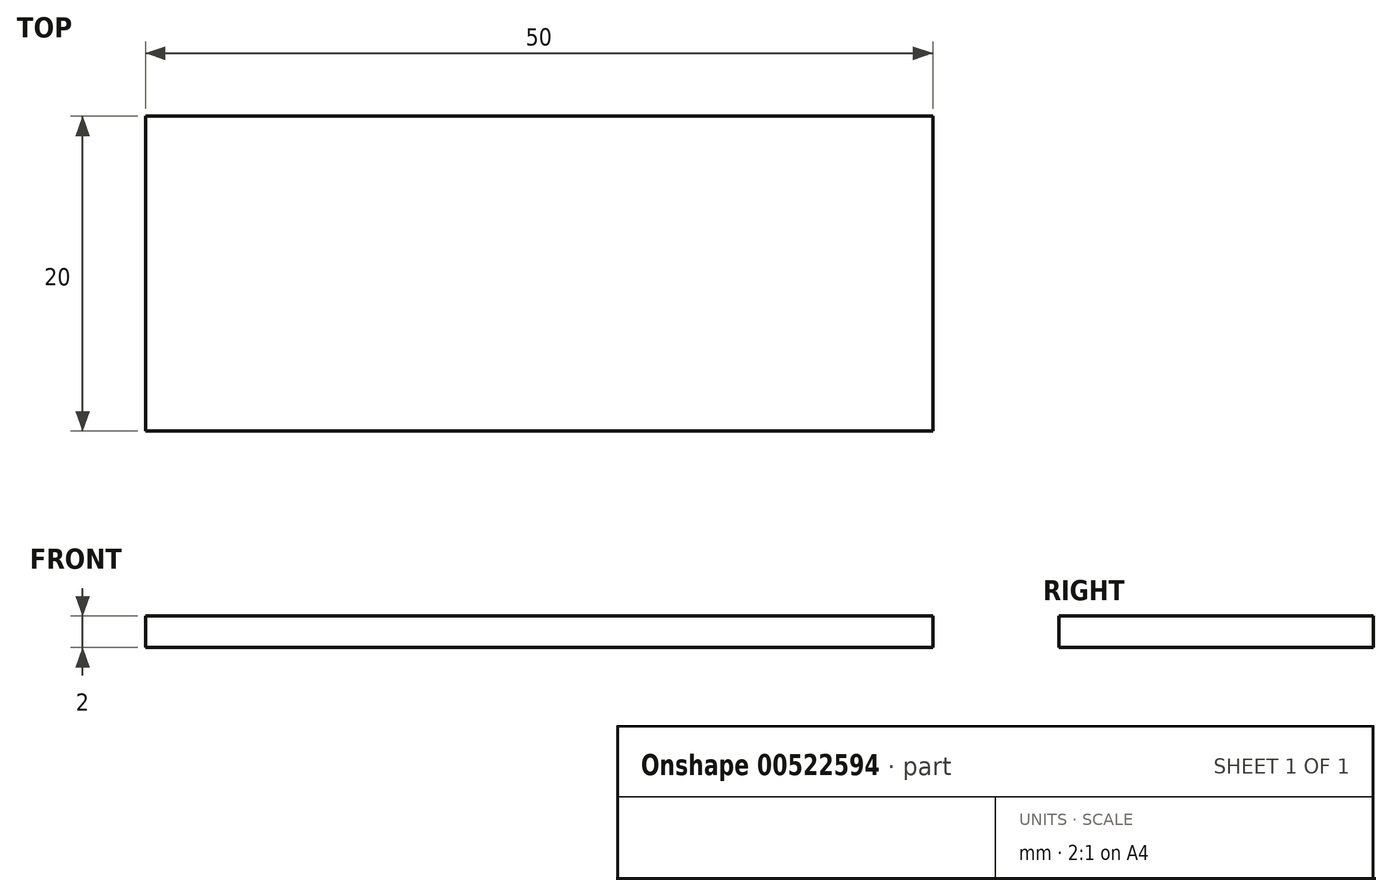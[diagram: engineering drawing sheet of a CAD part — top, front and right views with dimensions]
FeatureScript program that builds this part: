
annotation { "Feature Type Name" : "Feature", "Feature Type Description" : "" }
export const myFeature = defineFeature(function(context is Context, id is Id, definition is map)
    precondition{}
    {
        {
            var Q0;
            Q0=qCreatedBy(makeId("Top.planeOp"),FACE);
            var sketch = newSketch(context, id + "F0", { "sketchPlane" : qUnion([Q0])});
            skLineSegment(sketch, "E0.bottom", {"start": v(-25, 10) * mm, "end": v(25, 10) * mm});
            skLineSegment(sketch, "E0.top", {"start": v(-25, -10) * mm, "end": v(25, -10) * mm});
            skLineSegment(sketch, "E0.left", {"start": v(-25, 10) * mm, "end": v(-25, -10) * mm});
            skLineSegment(sketch, "E0.right", {"start": v(25, 10) * mm, "end": v(25, -10) * mm});
            skPoint(sketch, "E0.middle", {"position": v(0, 0) * mm});
            skSolve(sketch);
        }
        {
            var Q0;
            Q0=makeQuery(id+"F0.imprint","IMPRINT",FACE,{"disambiguationData":[TD([[makeQuery(id+"F0.imprint","IMPRINT",EDGE,{"derivedFrom":sQuery(id+"F0.wireOp",EDGE,"E0.bottom")}),-1.0]])]});
            extrude(context, id + "F1", {"entities" : qUnion([Q0]), "depth" : 2 * mm, "offsetDistance" : 25.4 * mm});
        }
    });
